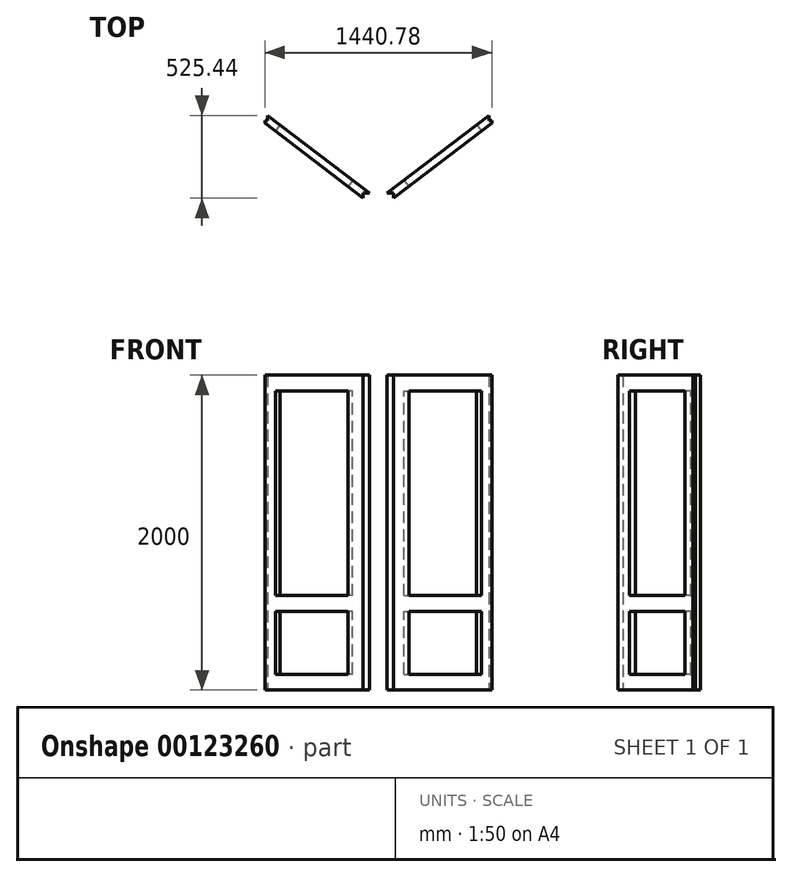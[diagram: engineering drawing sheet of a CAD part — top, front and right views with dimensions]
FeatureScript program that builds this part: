
annotation { "Feature Type Name" : "Feature", "Feature Type Description" : "" }
export const myFeature = defineFeature(function(context is Context, id is Id, definition is map)
    precondition{}
    {
        {
            var Q0;
            Q0=qCreatedBy(makeId("Top.planeOp"),FACE);
            var sketch = newSketch(context, id + "F0", { "sketchPlane" : qUnion([Q0])});
            skLineSegment(sketch, "E0.bottom", {"start": v(-302.5, 231.25) * mm, "end": v(302.5, 231.25) * mm, "construction": true});
            skLineSegment(sketch, "E0.top", {"start": v(-302.5, -231.25) * mm, "end": v(302.5, -231.25) * mm, "construction": true});
            skLineSegment(sketch, "E0.left", {"start": v(-302.5, 231.25) * mm, "end": v(-302.5, -231.25) * mm, "construction": true});
            skLineSegment(sketch, "E0.right", {"start": v(302.5, 231.25) * mm, "end": v(302.5, -231.25) * mm, "construction": true});
            skLineSegment(sketch, "E1", {"start": v(-302.5, 231.25) * mm, "end": v(302.5, -231.25) * mm, "construction": true});
            skLineSegment(sketch, "E2.bottom", {"start": v(-302.5, 231.25) * mm, "end": v(-320.39, 231.25) * mm, "construction": true});
            skLineSegment(sketch, "E2.top", {"start": v(-302.5, 356.25) * mm, "end": v(-427.5, 356.25) * mm, "construction": true});
            skLineSegment(sketch, "E2.right", {"start": v(-427.5, 231.25) * mm, "end": v(-427.5, 356.25) * mm, "construction": true});
            skLineSegment(sketch, "E3.bottom", {"start": v(302.5, -231.25) * mm, "end": v(402.5, -231.25) * mm, "construction": true});
            skLineSegment(sketch, "E3.top", {"start": v(302.5, -281.25) * mm, "end": v(402.5, -281.25) * mm, "construction": true});
            skLineSegment(sketch, "E3.left", {"start": v(302.5, -231.25) * mm, "end": v(302.5, -281.25) * mm, "construction": true});
            skLineSegment(sketch, "E3.right", {"start": v(402.5, -231.25) * mm, "end": v(402.5, -281.25) * mm, "construction": true});
            skPoint(sketch, "E4.middle", {"position": v(0, 0) * mm});
            skLineSegment(sketch, "E5", {"start": v(-320.39, 213.46) * mm, "end": v(302.5, -262.72) * mm});
            skLineSegment(sketch, "E6", {"start": v(-281.92, 246.98) * mm, "end": v(343.66, -231.25) * mm});
            skLineSegment(sketch, "E7", {"start": v(-320.39, 231.25) * mm, "end": v(-302.5, 231.25) * mm});
            skLineSegment(sketch, "E8", {"start": v(302.5, -231.25) * mm, "end": v(343.66, -231.25) * mm});
            skLineSegment(sketch, "E9", {"start": v(302.5, -231.25) * mm, "end": v(302.5, -262.72) * mm});
            skLineSegment(sketch, "E10.trimOffspring", {"start": v(-302.5, 262.72) * mm, "end": v(-302.5, 356.25) * mm, "construction": true});
            skPoint(sketch, "E11.end.orphan", {"position": v(-302.5, 246.98) * mm});
            skLineSegment(sketch, "E12", {"start": v(-302.5, 231.25) * mm, "end": v(-302.5, 262.72) * mm});
            skLineSegment(sketch, "E13", {"start": v(-302.5, 262.72) * mm, "end": v(-281.92, 246.98) * mm});
            skLineSegment(sketch, "E14", {"start": v(-320.39, 231.25) * mm, "end": v(-320.39, 213.46) * mm});
            skLineSegment(sketch, "E15.trimOffspring", {"start": v(-343.66, 231.25) * mm, "end": v(-427.5, 231.25) * mm, "construction": true});
            skSolve(sketch);
        }
        {
            var Q0;
            Q0=makeQuery(id+"F0.imprint","IMPRINT",FACE,{"disambiguationData":[TD([[makeQuery(id+"F0.imprint","IMPRINT",EDGE,{"derivedFrom":sQuery(id+"F0.wireOp",EDGE,"E5")}),1.0]])]});
            extrude(context, id + "F1", {"entities" : qUnion([Q0]), "depth" : 1000 * mm, "hasSecondDirection" : true, "secondDirectionOppositeDirection" : true, "secondDirectionDepth" : 1000 * mm});
        }
        {
            var Q0;
            Q0=makeQuery(id+"F1.opExtrude","CAP_EDGE",EDGE,{"disambiguationData":[OSD([sQuery(id+"F0.wireOp",EDGE,"E5")])],"isStart":false});
            var Q1;
            Q1=qCreatedBy(makeId("Right.planeOp"),FACE);
            cPlane(context, id + "F2", {"entities" : qUnion([Q0, Q1]), "cplaneType" : CPlaneType.LINE_ANGLE, "offset" : 25 * mm, "angle" : 0 * degree, "width" : 150 * mm, "height" : 150 * mm});
        }
        {
            var Q0;
            Q0=qCreatedBy(id+"F2.planeOp",FACE);
            var sketch = newSketch(context, id + "F3", { "sketchPlane" : qUnion([Q0])});
            skLineSegment(sketch, "E16.bottom", {"start": v(-301.66, 900) * mm, "end": v(278.99, 900) * mm});
            skLineSegment(sketch, "E16.top", {"start": v(-301.66, -400) * mm, "end": v(278.99, -400) * mm});
            skLineSegment(sketch, "E16.left", {"start": v(-301.66, 900) * mm, "end": v(-301.66, -400) * mm});
            skLineSegment(sketch, "E16.right", {"start": v(278.99, 900) * mm, "end": v(278.99, -400) * mm});
            skLineSegment(sketch, "E17.bottom", {"start": v(-301.66, -500) * mm, "end": v(278.99, -500) * mm});
            skLineSegment(sketch, "E17.top", {"start": v(-301.66, -900) * mm, "end": v(278.99, -900) * mm});
            skLineSegment(sketch, "E17.left", {"start": v(-301.66, -500) * mm, "end": v(-301.66, -900) * mm});
            skLineSegment(sketch, "E17.right", {"start": v(278.99, -500) * mm, "end": v(278.99, -900) * mm});
            skSolve(sketch);
        }
        {
            var Q0;
            Q0=makeQuery(id+"F3.imprint","IMPRINT",FACE,{"disambiguationData":[TD([[makeQuery(id+"F3.imprint","IMPRINT",EDGE,{"derivedFrom":sQuery(id+"F3.wireOp",EDGE,"E16.bottom")}),-1.0]])]});
            var Q1;
            Q1=makeQuery(id+"F3.imprint","IMPRINT",FACE,{"disambiguationData":[TD([[makeQuery(id+"F3.imprint","IMPRINT",EDGE,{"derivedFrom":sQuery(id+"F3.wireOp",EDGE,"E17.bottom")}),-1.0]])]});
            extrude(context, id + "F4", {"entities" : qUnion([Q0, Q1]), "operationType" : NewBodyOperationType.REMOVE, "endBound" : BoundingType.THROUGH_ALL, "oppositeDirection" : true, "depth" : 25 * mm});
        }
        {
            var Q0;
            Q0=qCreatedBy(makeId("Right.planeOp"),FACE);
            cPlane(context, id + "F5", {"entities" : qUnion([Q0]), "cplaneType" : CPlaneType.OFFSET, "offset" : 400 * mm, "width" : 150 * mm, "height" : 150 * mm});
        }
        {
            var Q0;
            Q0=makeQuery(id+"F1.opExtrude","SWEPT_BODY",BODY,{"disambiguationData":[OSD([sQuery(id+"F0.wireOp",EDGE,"E5"),sQuery(id+"F0.wireOp",EDGE,"E6"),sQuery(id+"F0.wireOp",EDGE,"E7"),sQuery(id+"F0.wireOp",EDGE,"E8"),sQuery(id+"F0.wireOp",EDGE,"E9"),sQuery(id+"F0.wireOp",EDGE,"E12"),sQuery(id+"F0.wireOp",EDGE,"E13"),sQuery(id+"F0.wireOp",EDGE,"E14")])]});
            var Q1;
            Q1=qCreatedBy(id+"F5.planeOp",FACE);
            mirror(context, id + "F6", {"entities" : qUnion([Q0]), "mirrorPlane" : qUnion([Q1])});
        }
    });
